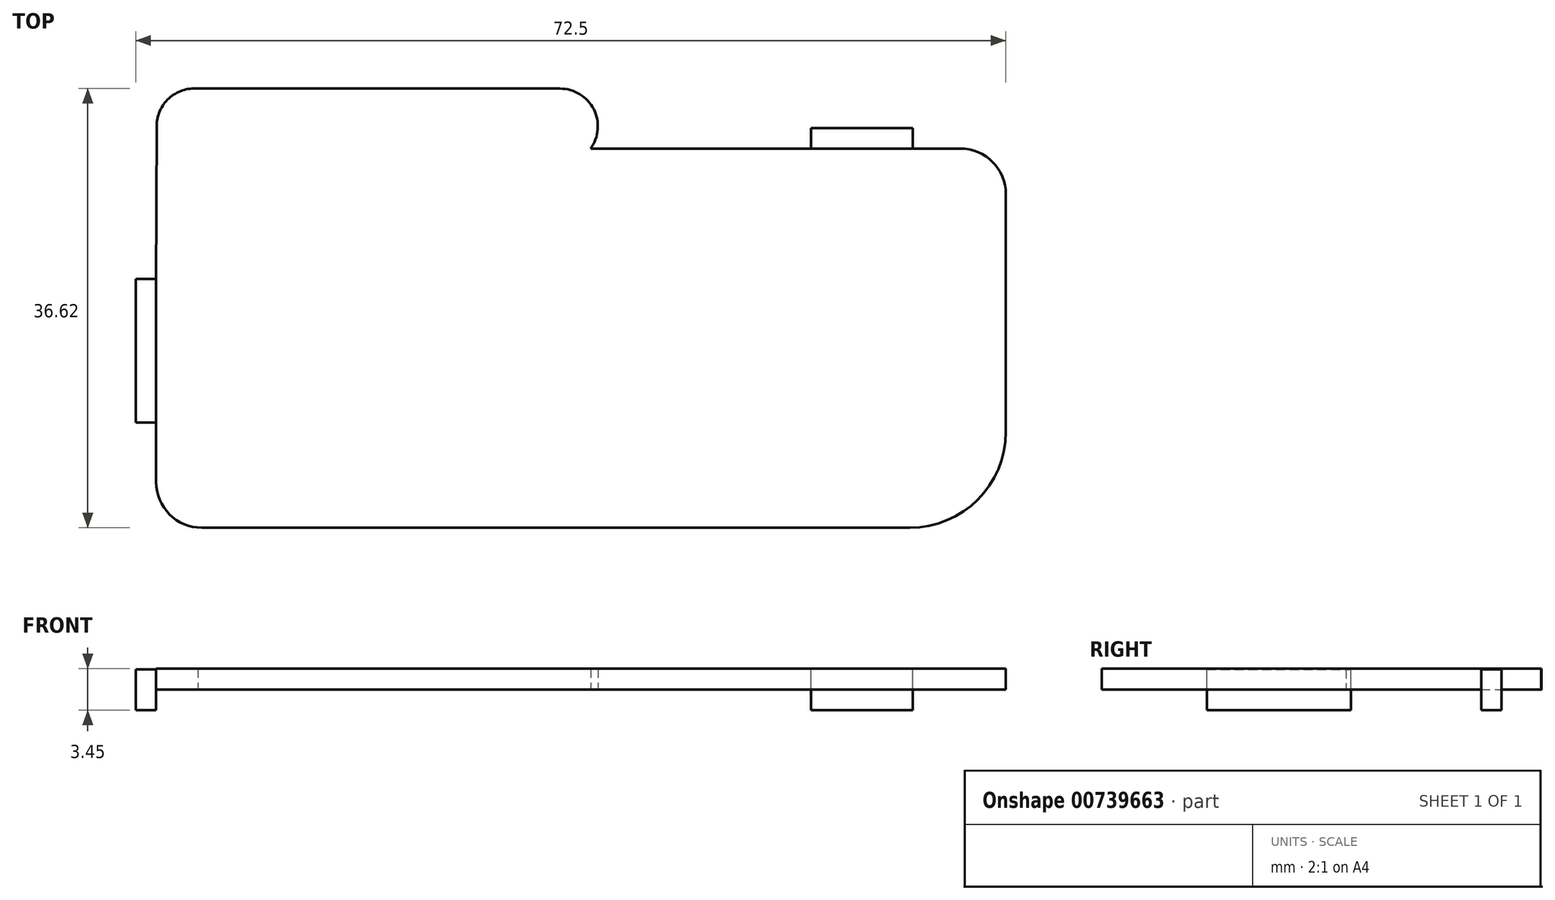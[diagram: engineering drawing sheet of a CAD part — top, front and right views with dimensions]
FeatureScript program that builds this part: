
annotation { "Feature Type Name" : "Feature", "Feature Type Description" : "" }
export const myFeature = defineFeature(function(context is Context, id is Id, definition is map)
    precondition{}
    {
        {
            var Q0;
            Q0=qCreatedBy(makeId("Top.planeOp"),FACE);
            var sketch = newSketch(context, id + "F0", { "sketchPlane" : qUnion([Q0])});
            skLineSegment(sketch, "E0.0.0", {"start": v(33.61, 9.63) * mm, "end": v(2.61, 9.63) * mm});
            skLineSegment(sketch, "E0.0.1", {"start": v(2.61, 9.63) * mm, "end": v(2.61, 12.28) * mm});
            skArc(sketch, "E0.0.2", {"start": v(2.61, 12.28) * mm, "mid": v(1.92, 13.95) * mm, "end": v(0.26, 14.63) * mm});
            skLineSegment(sketch, "E0.0.3", {"start": v(0.26, 14.63) * mm, "end": v(-29.95, 14.63) * mm});
            skArc(sketch, "E0.0.4", {"start": v(-29.95, 14.63) * mm, "mid": v(-31.77, 14.05) * mm, "end": v(-32.55, 12.3) * mm});
            skLineSegment(sketch, "E0.0.5", {"start": v(-32.55, 12.3) * mm, "end": v(-32.59, -0.84) * mm});
            skLineSegment(sketch, "E0.0.6", {"start": v(-32.59, -0.84) * mm, "end": v(-32.59, -17.37) * mm});
            skArc(sketch, "E0.0.7", {"start": v(-32.59, -17.37) * mm, "mid": v(-31.7, -19.49) * mm, "end": v(-29.59, -20.37) * mm});
            skLineSegment(sketch, "E0.0.8", {"start": v(-29.59, -20.37) * mm, "end": v(29.41, -20.37) * mm});
            skArc(sketch, "E0.0.9", {"start": v(29.41, -20.37) * mm, "mid": v(34.5, -18.26) * mm, "end": v(36.61, -13.17) * mm});
            skLineSegment(sketch, "E0.0.10", {"start": v(36.61, -13.17) * mm, "end": v(36.61, 6.63) * mm});
            skArc(sketch, "E0.0.11", {"start": v(36.61, 6.63) * mm, "mid": v(35.73, 8.76) * mm, "end": v(33.61, 9.63) * mm});
            skPoint(sketch, "E1", {"position": v(-29.07, 6.13) * mm});
            skArc(sketch, "E2.0", {"start": v(-33.39, -17.37) * mm, "mid": v(-32.27, -20.05) * mm, "end": v(-29.59, -21.17) * mm});
            skLineSegment(sketch, "E2.1", {"start": v(-33.39, -0.83) * mm, "end": v(-33.39, -17.37) * mm});
            skLineSegment(sketch, "E2.2", {"start": v(-33.35, 12.3) * mm, "end": v(-33.39, -0.83) * mm});
            skArc(sketch, "E2.3", {"start": v(-29.91, 15.43) * mm, "mid": v(-32.32, 14.63) * mm, "end": v(-33.35, 12.3) * mm});
            skLineSegment(sketch, "E2.4", {"start": v(0.26, 15.43) * mm, "end": v(-29.91, 15.43) * mm});
            skLineSegment(sketch, "E2.5", {"start": v(-29.59, -21.17) * mm, "end": v(29.41, -21.17) * mm});
            skArc(sketch, "E2.6", {"start": v(29.41, -21.17) * mm, "mid": v(35.07, -18.82) * mm, "end": v(37.41, -13.17) * mm});
            skLineSegment(sketch, "E2.7", {"start": v(37.41, -13.17) * mm, "end": v(37.41, 6.63) * mm});
            skArc(sketch, "E2.8", {"start": v(37.41, 6.63) * mm, "mid": v(36.3, 9.32) * mm, "end": v(33.61, 10.43) * mm});
            skLineSegment(sketch, "E2.9", {"start": v(33.61, 10.43) * mm, "end": v(2.81, 10.43) * mm});
            skArc(sketch, "E2.10", {"start": v(2.81, 10.43) * mm, "mid": v(3.07, 13.72) * mm, "end": v(0.26, 15.43) * mm});
            skSolve(sketch);
        }
        {
            var Q0;
            Q0=makeQuery(id+"F0.imprint","IMPRINT",FACE,{"disambiguationData":[TD([[makeQuery(id+"F0.imprint","IMPRINT",EDGE,{"derivedFrom":sQuery(id+"F0.wireOp",EDGE,"E0.0.0")}),-1.0]])]});
            var Q1;
            Q1=makeQuery(id+"F0.imprint","IMPRINT",FACE,{"disambiguationData":[TD([[makeQuery(id+"F0.imprint","IMPRINT",EDGE,{"derivedFrom":sQuery(id+"F0.wireOp",EDGE,"E0.0.0")}),1.0]])]});
            extrude(context, id + "F1", {"entities" : qUnion([Q0, Q1]), "depth" : 1.75 * mm, "offsetDistance" : 25 * mm});
        }
        {
            var Q0;
            Q0=makeQuery(id+"F1.opExtrude","CAP_FACE",FACE,{"disambiguationData":[OSD([sQuery(id+"F0.wireOp",EDGE,"E2.0"),sQuery(id+"F0.wireOp",EDGE,"E2.1"),sQuery(id+"F0.wireOp",EDGE,"E2.2"),sQuery(id+"F0.wireOp",EDGE,"E2.3"),sQuery(id+"F0.wireOp",EDGE,"E2.4"),sQuery(id+"F0.wireOp",EDGE,"E2.5"),sQuery(id+"F0.wireOp",EDGE,"E2.6"),sQuery(id+"F0.wireOp",EDGE,"E2.7"),sQuery(id+"F0.wireOp",EDGE,"E2.8"),sQuery(id+"F0.wireOp",EDGE,"E2.9"),sQuery(id+"F0.wireOp",EDGE,"E2.10")])],"isStart":true});
            var sketch = newSketch(context, id + "F2", { "sketchPlane" : qUnion([Q0])});
            skLineSegment(sketch, "E3.bottom", {"start": v(29.66, -10.43) * mm, "end": v(21.16, -10.43) * mm});
            skLineSegment(sketch, "E3.top", {"start": v(29.66, -12.13) * mm, "end": v(21.16, -12.13) * mm});
            skLineSegment(sketch, "E3.left", {"start": v(29.66, -10.43) * mm, "end": v(29.66, -12.13) * mm});
            skLineSegment(sketch, "E3.right", {"start": v(21.16, -10.43) * mm, "end": v(21.16, -12.13) * mm});
            skLineSegment(sketch, "E4.bottom", {"start": v(-33.39, 12.42) * mm, "end": v(-35.09, 12.42) * mm});
            skLineSegment(sketch, "E4.top", {"start": v(-33.39, 0.42) * mm, "end": v(-35.09, 0.42) * mm});
            skLineSegment(sketch, "E4.left", {"start": v(-33.39, 12.42) * mm, "end": v(-33.39, 0.42) * mm});
            skLineSegment(sketch, "E4.right", {"start": v(-35.09, 12.42) * mm, "end": v(-35.09, 0.42) * mm});
            skSolve(sketch);
        }
        {
            var Q0;
            Q0 = qSketchRegion(id + "F2", true);
            extrude(context, id + "F3", {"entities" : qUnion([Q0]), "operationType" : NewBodyOperationType.ADD, "endBound" : BoundingType.SYMMETRIC, "depth" : 3.4 * mm, "offsetDistance" : 25 * mm});
        }
    });
